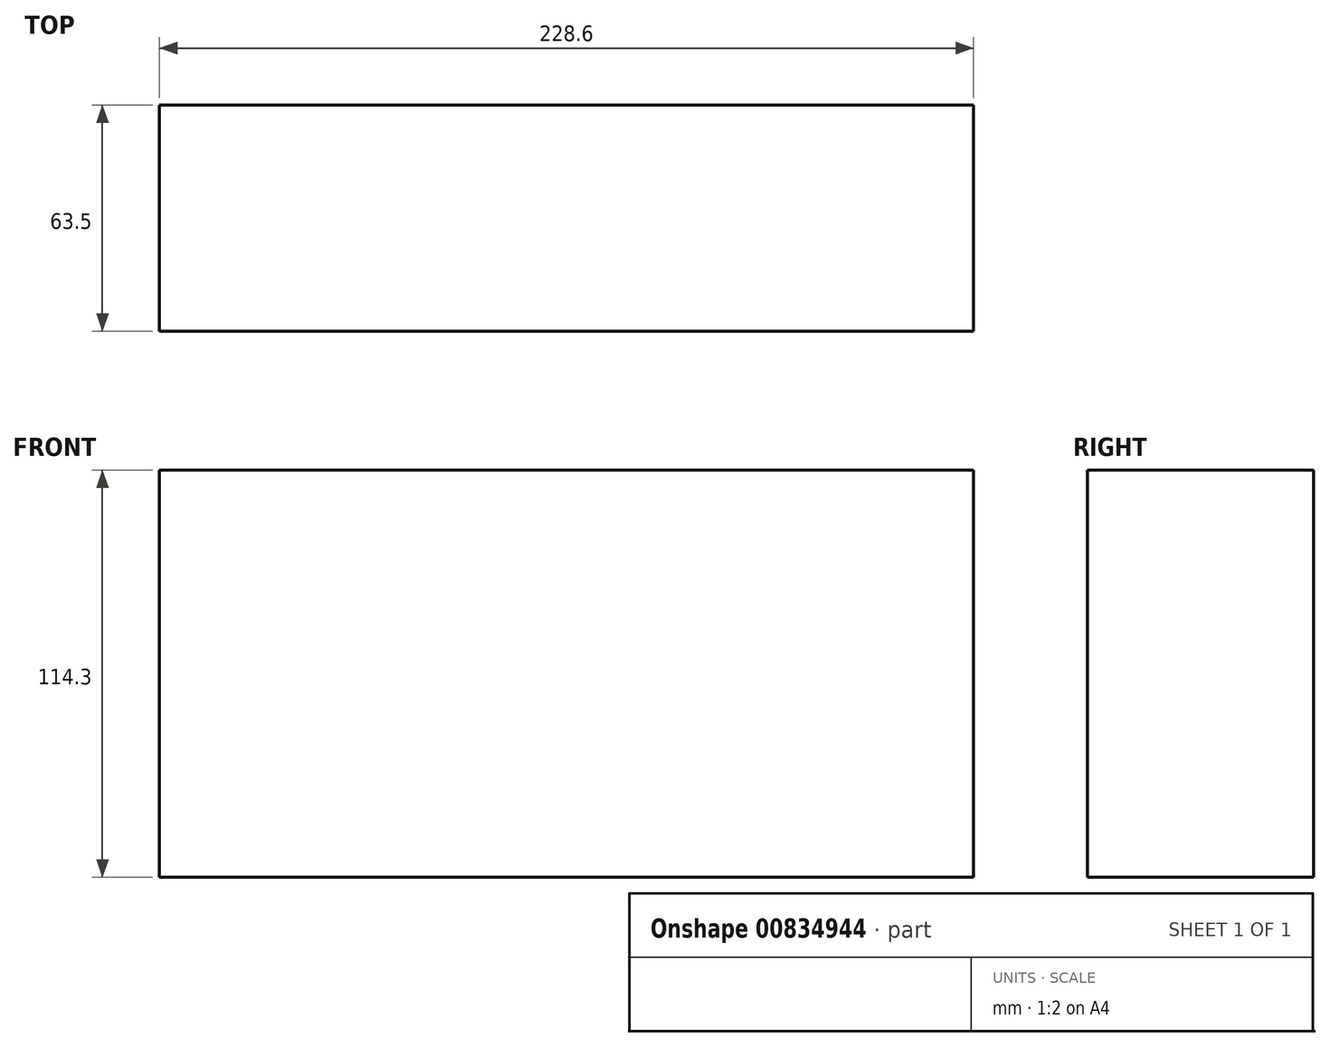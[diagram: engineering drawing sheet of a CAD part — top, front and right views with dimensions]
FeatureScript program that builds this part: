
annotation { "Feature Type Name" : "Feature", "Feature Type Description" : "" }
export const myFeature = defineFeature(function(context is Context, id is Id, definition is map)
    precondition{}
    {
        {
            var Q0;
            Q0=qCreatedBy(makeId("Top.planeOp"),FACE);
            var sketch = newSketch(context, id + "F0", { "sketchPlane" : qUnion([Q0])});
            skLineSegment(sketch, "E0.bottom", {"start": v(0, 0) * mm, "end": v(228.6, 0) * mm});
            skLineSegment(sketch, "E0.top", {"start": v(0, 63.5) * mm, "end": v(228.6, 63.5) * mm});
            skLineSegment(sketch, "E0.left", {"start": v(0, 0) * mm, "end": v(0, 63.5) * mm});
            skLineSegment(sketch, "E0.right", {"start": v(228.6, 0) * mm, "end": v(228.6, 63.5) * mm});
            skSolve(sketch);
        }
        {
            var Q0;
            Q0=qSketchRegion(id+"F0",true);
            extrude(context, id + "F1", {"entities" : qUnion([Q0]), "depth" : 114.3 * mm, "offsetDistance" : 25.4 * mm});
        }
    });
